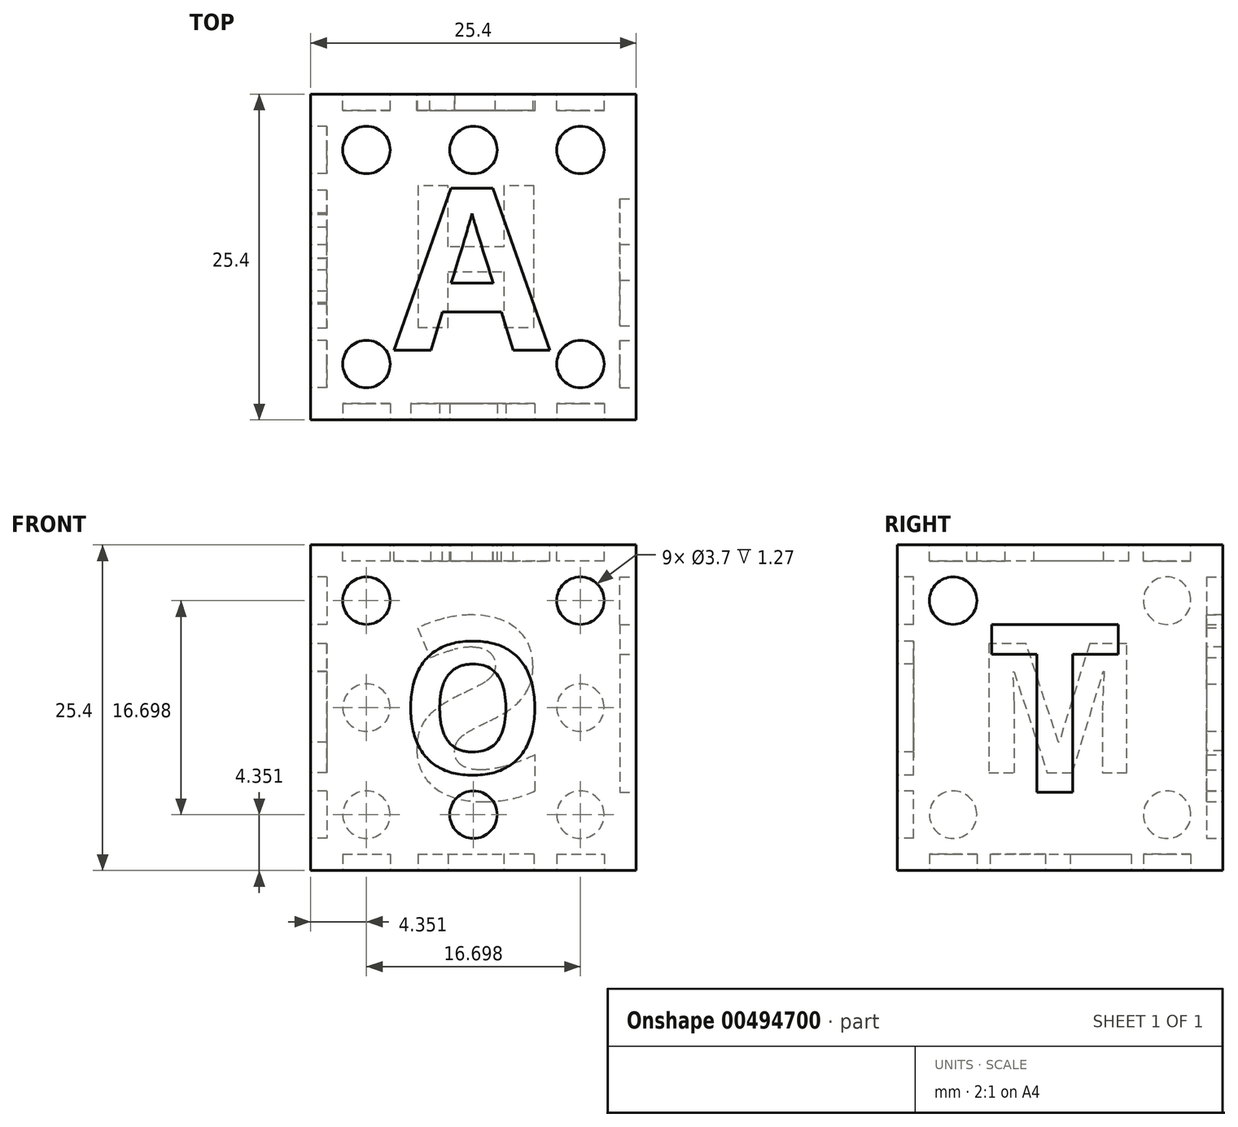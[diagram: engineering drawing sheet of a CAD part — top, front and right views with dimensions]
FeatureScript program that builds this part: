
annotation { "Feature Type Name" : "Feature", "Feature Type Description" : "" }
export const myFeature = defineFeature(function(context is Context, id is Id, definition is map)
    precondition{}
    {
        {
            var Q0;
            Q0=qCreatedBy(makeId("Top.planeOp"),FACE);
            var sketch = newSketch(context, id + "F0", { "sketchPlane" : qUnion([Q0])});
            skLineSegment(sketch, "E0.bottom", {"start": v(0, 0) * mm, "end": v(25.4, 0) * mm});
            skLineSegment(sketch, "E0.top", {"start": v(0, -25.4) * mm, "end": v(25.4, -25.4) * mm});
            skLineSegment(sketch, "E0.left", {"start": v(0, 0) * mm, "end": v(0, -25.4) * mm});
            skLineSegment(sketch, "E0.right", {"start": v(25.4, 0) * mm, "end": v(25.4, -25.4) * mm});
            skSolve(sketch);
        }
        {
            var Q0;
            Q0 = qSketchRegion(id + "F0", true);
            extrude(context, id + "F1", {"entities" : qUnion([Q0]), "depth" : 25.4 * mm});
        }
        {
            var Q0;
            Q0=makeQuery(id+"F1.opExtrude","SWEPT_FACE",FACE,{"disambiguationData":[OSD([sQuery(id+"F0.wireOp",EDGE,"E0.right")])]});
            var sketch = newSketch(context, id + "F2", { "sketchPlane" : qUnion([Q0])});
            skText(sketch, "E1", { "text": "T", "fontName": "OpenSans-Bold.ttf"});
            skLineSegment(sketch, "E2", {"start": v(-6.99, 12.7) * mm, "end": v(0, 12.7) * mm, "construction": true});
            skLineSegment(sketch, "E3", {"start": v(-12.7, 19.3) * mm, "end": v(-12.7, 25.4) * mm, "construction": true});
            skLineSegment(sketch, "E4", {"start": v(-18.42, 8.45) * mm, "end": v(-25.4, 8.45) * mm, "construction": true});
            skLineSegment(sketch, "E5", {"start": v(-12.7, 6.1) * mm, "end": v(-12.7, 0) * mm, "construction": true});
            skCircle(sketch, "E6", {"center": v(-21.05, 21.05) * mm, "radius": 1.85 * mm});
            skLineSegment(sketch, "E7.bottom", {"start": v(-22.9, 22.9) * mm, "end": v(-2.5, 22.9) * mm, "construction": true});
            skLineSegment(sketch, "E7.top", {"start": v(-22.9, 2.5) * mm, "end": v(-2.5, 2.5) * mm, "construction": true});
            skLineSegment(sketch, "E7.left", {"start": v(-22.9, 22.9) * mm, "end": v(-22.9, 2.5) * mm, "construction": true});
            skLineSegment(sketch, "E7.right", {"start": v(-2.5, 22.9) * mm, "end": v(-2.5, 2.5) * mm, "construction": true});
            const initialGuessF2  = {"E1": [-0.01842, 0.0061, 1, 0, 0.0132]};
            skSetInitialGuess(sketch, initialGuessF2);
            skSolve(sketch);
        }
        {
            var Q0;
            Q0=makeQuery(id+"F1.opExtrude","CAP_FACE",FACE,{"disambiguationData":[OSD([sQuery(id+"F0.wireOp",EDGE,"E0.bottom"),sQuery(id+"F0.wireOp",EDGE,"E0.top"),sQuery(id+"F0.wireOp",EDGE,"E0.left"),sQuery(id+"F0.wireOp",EDGE,"E0.right")])],"isStart":true});
            var sketch = newSketch(context, id + "F3", { "sketchPlane" : qUnion([Q0])});
            skText(sketch, "E8", { "text": "H", "fontName": "OpenSans-Bold.ttf"});
            skLineSegment(sketch, "E9", {"start": v(18.41, 12.7) * mm, "end": v(25.4, 12.7) * mm, "construction": true});
            skPoint(sketch, "E9.startSnap0", {"position": v(25.4, 12.7) * mm});
            skLineSegment(sketch, "E10", {"start": v(6.98, 12.7) * mm, "end": v(0, 12.7) * mm, "construction": true});
            skPoint(sketch, "E10.startSnap0", {"position": v(6.98, 12.7) * mm});
            skLineSegment(sketch, "E11", {"start": v(12.7, 18.26) * mm, "end": v(12.7, 25.4) * mm, "construction": true});
            skLineSegment(sketch, "E12", {"start": v(12.7, 25.4) * mm, "end": v(12.74, 25.95) * mm, "construction": true});
            skLineSegment(sketch, "E13", {"start": v(12.7, 7.14) * mm, "end": v(12.7, 0) * mm, "construction": true});
            skCircle(sketch, "E14", {"center": v(4.35, 21.05) * mm, "radius": 1.85 * mm});
            skCircle(sketch, "E15", {"center": v(21.05, 4.35) * mm, "radius": 1.85 * mm});
            skLineSegment(sketch, "E16.bottom", {"start": v(2.5, 22.9) * mm, "end": v(22.9, 22.9) * mm, "construction": true});
            skLineSegment(sketch, "E16.top", {"start": v(2.5, 2.5) * mm, "end": v(22.9, 2.5) * mm, "construction": true});
            skLineSegment(sketch, "E16.left", {"start": v(2.5, 22.9) * mm, "end": v(2.5, 2.5) * mm, "construction": true});
            skLineSegment(sketch, "E16.right", {"start": v(22.9, 22.9) * mm, "end": v(22.9, 2.5) * mm, "construction": true});
            const initialGuessF3  = {"E8": [0.00698, 0.00714, 1, 0, 0.01113]};
            skSetInitialGuess(sketch, initialGuessF3);
            skSolve(sketch);
        }
        {
            var Q0;
            Q0=makeQuery(id+"F1.opExtrude","SWEPT_FACE",FACE,{"disambiguationData":[OSD([sQuery(id+"F0.wireOp",EDGE,"E0.top")])]});
            var sketch = newSketch(context, id + "F4", { "sketchPlane" : qUnion([Q0])});
            skText(sketch, "E17", { "text": "O", "fontName": "OpenSans-Bold.ttf"});
            skLineSegment(sketch, "E18", {"start": v(12.7, 17.83) * mm, "end": v(12.7, 25.4) * mm, "construction": true});
            skLineSegment(sketch, "E19", {"start": v(18.41, 12.7) * mm, "end": v(25.4, 12.7) * mm, "construction": true});
            skLineSegment(sketch, "E20", {"start": v(25.4, 12.7) * mm, "end": v(25.78, 13.36) * mm, "construction": true});
            skLineSegment(sketch, "E21", {"start": v(12.7, 7.57) * mm, "end": v(12.7, 0) * mm, "construction": true});
            skLineSegment(sketch, "E22", {"start": v(12.7, 0) * mm, "end": v(12.7, -0.66) * mm, "construction": true});
            skLineSegment(sketch, "E23", {"start": v(6.98, 12.7) * mm, "end": v(0, 12.7) * mm, "construction": true});
            skCircle(sketch, "E24", {"center": v(4.35, 21.05) * mm, "radius": 1.85 * mm});
            skCircle(sketch, "E25", {"center": v(21.05, 21.05) * mm, "radius": 1.85 * mm});
            skPoint(sketch, "E26", {"position": v(12.7, 21.61) * mm});
            skLineSegment(sketch, "E27.top", {"start": v(4.64, 25.4) * mm, "end": v(0, 25.4) * mm, "construction": true});
            skLineSegment(sketch, "E27.right", {"start": v(0, 21.61) * mm, "end": v(0, 25.4) * mm, "construction": true});
            skLineSegment(sketch, "E28.top", {"start": v(20.76, 25.4) * mm, "end": v(25.4, 25.4) * mm, "construction": true});
            skLineSegment(sketch, "E28.right", {"start": v(25.4, 21.61) * mm, "end": v(25.4, 25.4) * mm, "construction": true});
            skCircle(sketch, "E29", {"center": v(12.7, 4.35) * mm, "radius": 1.85 * mm});
            skPoint(sketch, "E30.firstSnap0", {"position": v(2.5, 20.98) * mm});
            skLineSegment(sketch, "E30.bottom", {"start": v(2.5, 22.9) * mm, "end": v(22.9, 22.9) * mm, "construction": true});
            skLineSegment(sketch, "E30.top", {"start": v(2.5, 2.5) * mm, "end": v(22.9, 2.5) * mm, "construction": true});
            skLineSegment(sketch, "E30.left", {"start": v(2.5, 22.9) * mm, "end": v(2.5, 2.5) * mm, "construction": true});
            skLineSegment(sketch, "E30.right", {"start": v(22.9, 22.9) * mm, "end": v(22.9, 2.5) * mm, "construction": true});
            const initialGuessF4  = {"E17": [0.00698, 0.00757, 1, 0, 0.01025]};
            skSetInitialGuess(sketch, initialGuessF4);
            skSolve(sketch);
        }
        {
            var Q0;
            Q0=makeQuery(id+"F1.opExtrude","SWEPT_FACE",FACE,{"disambiguationData":[OSD([sQuery(id+"F0.wireOp",EDGE,"E0.left")])]});
            var sketch = newSketch(context, id + "F5", { "sketchPlane" : qUnion([Q0])});
            skText(sketch, "E31", { "text": "M", "fontName": "OpenSans-Bold.ttf"});
            skLineSegment(sketch, "E32", {"start": v(12.7, 17.78) * mm, "end": v(12.7, 25.4) * mm, "construction": true});
            skLineSegment(sketch, "E33", {"start": v(19.18, 7.17) * mm, "end": v(25.4, 7.17) * mm, "construction": true});
            skLineSegment(sketch, "E34", {"start": v(6.22, 7.17) * mm, "end": v(0, 7.17) * mm, "construction": true});
            skLineSegment(sketch, "E35", {"start": v(12.7, 7.62) * mm, "end": v(12.7, 0) * mm, "construction": true});
            skCircle(sketch, "E36", {"center": v(21.05, 21.05) * mm, "radius": 1.85 * mm});
            skCircle(sketch, "E37", {"center": v(4.35, 21.05) * mm, "radius": 1.85 * mm});
            skCircle(sketch, "E38", {"center": v(4.35, 4.35) * mm, "radius": 1.85 * mm});
            skCircle(sketch, "E39", {"center": v(21.05, 4.35) * mm, "radius": 1.85 * mm});
            skLineSegment(sketch, "E40", {"start": v(0, 20.74) * mm, "end": v(0.09, 21.93) * mm, "construction": true});
            skLineSegment(sketch, "E41", {"start": v(25.4, 4.66) * mm, "end": v(25.62, 3.31) * mm, "construction": true});
            skPoint(sketch, "E42.oppositeSnap0", {"position": v(22.9, 4.66) * mm});
            skLineSegment(sketch, "E42.bottom", {"start": v(2.5, 22.9) * mm, "end": v(22.9, 22.9) * mm, "construction": true});
            skLineSegment(sketch, "E42.top", {"start": v(2.5, 2.5) * mm, "end": v(22.9, 2.5) * mm, "construction": true});
            skLineSegment(sketch, "E42.left", {"start": v(2.5, 22.9) * mm, "end": v(2.5, 2.5) * mm, "construction": true});
            skLineSegment(sketch, "E42.right", {"start": v(22.9, 22.9) * mm, "end": v(22.9, 2.5) * mm, "construction": true});
            const initialGuessF5  = {"E31": [0.00622, 0.00762, 1, 0, 0.01016]};
            skSetInitialGuess(sketch, initialGuessF5);
            skSolve(sketch);
        }
        {
            var Q0;
            Q0=makeQuery(id+"F1.opExtrude","CAP_FACE",FACE,{"disambiguationData":[OSD([sQuery(id+"F0.wireOp",EDGE,"E0.bottom"),sQuery(id+"F0.wireOp",EDGE,"E0.top"),sQuery(id+"F0.wireOp",EDGE,"E0.left"),sQuery(id+"F0.wireOp",EDGE,"E0.right")])],"isStart":false});
            var sketch = newSketch(context, id + "F6", { "sketchPlane" : qUnion([Q0])});
            skText(sketch, "E43", { "text": "A", "fontName": "OpenSans-Bold.ttf"});
            skCircle(sketch, "E44", {"center": v(21.05, -4.35) * mm, "radius": 1.85 * mm});
            skCircle(sketch, "E45", {"center": v(4.35, -4.35) * mm, "radius": 1.85 * mm});
            skCircle(sketch, "E46", {"center": v(12.7, -4.35) * mm, "radius": 1.85 * mm});
            skCircle(sketch, "E47", {"center": v(4.35, -21.05) * mm, "radius": 1.85 * mm});
            skCircle(sketch, "E48", {"center": v(21.05, -21.05) * mm, "radius": 1.85 * mm});
            skPoint(sketch, "E49", {"position": v(21.05, -12.02) * mm});
            skLineSegment(sketch, "E50.bottom", {"start": v(2.5, -2.5) * mm, "end": v(22.9, -2.5) * mm, "construction": true});
            skLineSegment(sketch, "E50.top", {"start": v(2.5, -22.9) * mm, "end": v(22.9, -22.9) * mm, "construction": true});
            skLineSegment(sketch, "E50.left", {"start": v(2.5, -2.5) * mm, "end": v(2.5, -22.9) * mm, "construction": true});
            skLineSegment(sketch, "E50.right", {"start": v(22.9, -2.5) * mm, "end": v(22.9, -22.9) * mm, "construction": true});
            const initialGuessF6  = {"E43": [0.0065, -0.01998, 1, 0, 0.0127]};
            skSetInitialGuess(sketch, initialGuessF6);
            skSolve(sketch);
        }
        {
            var Q0;
            Q0=makeQuery(id+"F1.opExtrude","SWEPT_FACE",FACE,{"disambiguationData":[OSD([sQuery(id+"F0.wireOp",EDGE,"E0.bottom")])]});
            var sketch = newSketch(context, id + "F7", { "sketchPlane" : qUnion([Q0])});
            skText(sketch, "E51", { "text": "S", "fontName": "OpenSans-Bold.ttf"});
            skLineSegment(sketch, "E52", {"start": v(-25.4, 12.7) * mm, "end": v(-25.57, 13.09) * mm, "construction": true});
            skCircle(sketch, "E53", {"center": v(-21.05, 21.05) * mm, "radius": 1.85 * mm});
            skCircle(sketch, "E54", {"center": v(-4.35, 21.05) * mm, "radius": 1.85 * mm});
            skCircle(sketch, "E55", {"center": v(-4.35, 12.7) * mm, "radius": 1.85 * mm});
            skCircle(sketch, "E56", {"center": v(-21.05, 4.35) * mm, "radius": 1.85 * mm});
            skCircle(sketch, "E57", {"center": v(-4.35, 4.35) * mm, "radius": 1.85 * mm});
            skCircle(sketch, "E58", {"center": v(-21.05, 12.7) * mm, "radius": 1.85 * mm});
            skLineSegment(sketch, "E59.bottom", {"start": v(-22.9, 22.9) * mm, "end": v(-2.5, 22.9) * mm, "construction": true});
            skLineSegment(sketch, "E59.top", {"start": v(-22.9, 2.5) * mm, "end": v(-2.5, 2.5) * mm, "construction": true});
            skLineSegment(sketch, "E59.left", {"start": v(-22.9, 22.9) * mm, "end": v(-22.9, 2.5) * mm, "construction": true});
            skLineSegment(sketch, "E59.right", {"start": v(-2.5, 22.9) * mm, "end": v(-2.5, 2.5) * mm, "construction": true});
            skLineSegment(sketch, "E60", {"start": v(0, 12.7) * mm, "end": v(-25.4, 12.7) * mm, "construction": true});
            const initialGuessF7  = {"E51": [-0.01842, 0.00556, 1, 0, 0.01429]};
            skSetInitialGuess(sketch, initialGuessF7);
            skSolve(sketch);
        }
        {
            var Q0;
            Q0 = qSketchRegion(id + "F2", true);
            extrude(context, id + "F8", {"entities" : qUnion([Q0]), "operationType" : NewBodyOperationType.REMOVE, "oppositeDirection" : true, "depth" : 1.27 * mm});
        }
        {
            var Q0;
            Q0=makeQuery(id+"F7.imprint","IMPRINT",FACE,{"disambiguationData":[TD([[makeQuery(id+"F7.imprint","IMPRINT",EDGE,{"derivedFrom":sQuery(id+"F7.wireOp",EDGE,"E51.sketch_text.stroke-0")}),-1.0]])]});
            var Q1;
            Q1=makeQuery(id+"F7.imprint","IMPRINT",FACE,{"disambiguationData":[TD([[makeQuery(id+"F7.imprint","IMPRINT",EDGE,{"derivedFrom":sQuery(id+"F7.wireOp",EDGE,"E55")}),1.0]])]});
            var Q2;
            Q2=makeQuery(id+"F7.imprint","IMPRINT",FACE,{"disambiguationData":[TD([[makeQuery(id+"F7.imprint","IMPRINT",EDGE,{"derivedFrom":sQuery(id+"F7.wireOp",EDGE,"E58")}),1.0]])]});
            var Q3;
            Q3=makeQuery(id+"F7.imprint","IMPRINT",FACE,{"disambiguationData":[TD([[makeQuery(id+"F7.imprint","IMPRINT",EDGE,{"derivedFrom":sQuery(id+"F7.wireOp",EDGE,"E56")}),1.0]])]});
            var Q4;
            Q4=makeQuery(id+"F7.imprint","IMPRINT",FACE,{"disambiguationData":[TD([[makeQuery(id+"F7.imprint","IMPRINT",EDGE,{"derivedFrom":sQuery(id+"F7.wireOp",EDGE,"E53")}),1.0]])]});
            var Q5;
            Q5=makeQuery(id+"F7.imprint","IMPRINT",FACE,{"disambiguationData":[TD([[makeQuery(id+"F7.imprint","IMPRINT",EDGE,{"derivedFrom":sQuery(id+"F7.wireOp",EDGE,"E54")}),1.0]])]});
            var Q6;
            Q6=makeQuery(id+"F7.imprint","IMPRINT",FACE,{"disambiguationData":[TD([[makeQuery(id+"F7.imprint","IMPRINT",EDGE,{"derivedFrom":sQuery(id+"F7.wireOp",EDGE,"E57")}),1.0]])]});
            extrude(context, id + "F9", {"entities" : qUnion([Q0, Q1, Q2, Q3, Q4, Q5, Q6]), "operationType" : NewBodyOperationType.REMOVE, "oppositeDirection" : true, "depth" : 1.27 * mm});
        }
        {
            var Q0;
            Q0=makeQuery(id+"F6.imprint","IMPRINT",FACE,{"disambiguationData":[TD([[makeQuery(id+"F6.imprint","IMPRINT",EDGE,{"derivedFrom":sQuery(id+"F6.wireOp",EDGE,"E48")}),1.0]])]});
            var Q1;
            Q1=makeQuery(id+"F6.imprint","IMPRINT",FACE,{"disambiguationData":[TD([[makeQuery(id+"F6.imprint","IMPRINT",EDGE,{"derivedFrom":sQuery(id+"F6.wireOp",EDGE,"E44")}),1.0]])]});
            var Q2;
            Q2=makeQuery(id+"F6.imprint","IMPRINT",FACE,{"disambiguationData":[TD([[makeQuery(id+"F6.imprint","IMPRINT",EDGE,{"derivedFrom":sQuery(id+"F6.wireOp",EDGE,"E46")}),1.0]])]});
            var Q3;
            Q3=makeQuery(id+"F6.imprint","IMPRINT",FACE,{"disambiguationData":[TD([[makeQuery(id+"F6.imprint","IMPRINT",EDGE,{"derivedFrom":sQuery(id+"F6.wireOp",EDGE,"E45")}),1.0]])]});
            var Q4;
            Q4=makeQuery(id+"F6.imprint","IMPRINT",FACE,{"disambiguationData":[TD([[makeQuery(id+"F6.imprint","IMPRINT",EDGE,{"derivedFrom":sQuery(id+"F6.wireOp",EDGE,"E43.sketch_text.stroke-0")}),-1.0]])]});
            var Q5;
            Q5=makeQuery(id+"F6.imprint","IMPRINT",FACE,{"disambiguationData":[TD([[makeQuery(id+"F6.imprint","IMPRINT",EDGE,{"derivedFrom":sQuery(id+"F6.wireOp",EDGE,"E47")}),1.0]])]});
            extrude(context, id + "F10", {"entities" : qUnion([Q0, Q1, Q2, Q3, Q4, Q5]), "operationType" : NewBodyOperationType.REMOVE, "oppositeDirection" : true, "depth" : 1.27 * mm});
        }
        {
            var Q0;
            Q0=makeQuery(id+"F3.imprint","IMPRINT",FACE,{"disambiguationData":[TD([[makeQuery(id+"F3.imprint","IMPRINT",EDGE,{"derivedFrom":sQuery(id+"F3.wireOp",EDGE,"E8.sketch_text.stroke-0")}),-1.0]])]});
            var Q1;
            Q1=makeQuery(id+"F3.imprint","IMPRINT",FACE,{"disambiguationData":[TD([[makeQuery(id+"F3.imprint","IMPRINT",EDGE,{"derivedFrom":sQuery(id+"F3.wireOp",EDGE,"E15")}),1.0]])]});
            var Q2;
            Q2=makeQuery(id+"F3.imprint","IMPRINT",FACE,{"disambiguationData":[TD([[makeQuery(id+"F3.imprint","IMPRINT",EDGE,{"derivedFrom":sQuery(id+"F3.wireOp",EDGE,"E14")}),1.0]])]});
            extrude(context, id + "F11", {"entities" : qUnion([Q0, Q1, Q2]), "operationType" : NewBodyOperationType.REMOVE, "oppositeDirection" : true, "depth" : 1.27 * mm});
        }
        {
            var Q0;
            Q0=makeQuery(id+"F5.imprint","IMPRINT",FACE,{"disambiguationData":[TD([[makeQuery(id+"F5.imprint","IMPRINT",EDGE,{"derivedFrom":sQuery(id+"F5.wireOp",EDGE,"E38")}),1.0]])]});
            var Q1;
            Q1=makeQuery(id+"F5.imprint","IMPRINT",FACE,{"disambiguationData":[TD([[makeQuery(id+"F5.imprint","IMPRINT",EDGE,{"derivedFrom":sQuery(id+"F5.wireOp",EDGE,"E39")}),1.0]])]});
            var Q2;
            Q2=makeQuery(id+"F5.imprint","IMPRINT",FACE,{"disambiguationData":[TD([[makeQuery(id+"F5.imprint","IMPRINT",EDGE,{"derivedFrom":sQuery(id+"F5.wireOp",EDGE,"E37")}),1.0]])]});
            var Q3;
            Q3=makeQuery(id+"F5.imprint","IMPRINT",FACE,{"disambiguationData":[TD([[makeQuery(id+"F5.imprint","IMPRINT",EDGE,{"derivedFrom":sQuery(id+"F5.wireOp",EDGE,"E36")}),1.0]])]});
            var Q4;
            Q4=makeQuery(id+"F5.imprint","IMPRINT",FACE,{"disambiguationData":[TD([[makeQuery(id+"F5.imprint","IMPRINT",EDGE,{"derivedFrom":sQuery(id+"F5.wireOp",EDGE,"E31.sketch_text.stroke-0")}),-1.0]])]});
            extrude(context, id + "F12", {"entities" : qUnion([Q0, Q1, Q2, Q3, Q4]), "operationType" : NewBodyOperationType.REMOVE, "oppositeDirection" : true, "depth" : 1.27 * mm});
        }
        {
            var Q0;
            Q0=makeQuery(id+"F4.imprint","IMPRINT",FACE,{"disambiguationData":[TD([[makeQuery(id+"F4.imprint","IMPRINT",EDGE,{"derivedFrom":sQuery(id+"F4.wireOp",EDGE,"E17.sketch_text.stroke-0")}),-1.0]])]});
            var Q1;
            Q1=makeQuery(id+"F4.imprint","IMPRINT",FACE,{"disambiguationData":[TD([[makeQuery(id+"F4.imprint","IMPRINT",EDGE,{"derivedFrom":sQuery(id+"F4.wireOp",EDGE,"E29")}),1.0]])]});
            var Q2;
            Q2=makeQuery(id+"F4.imprint","IMPRINT",FACE,{"disambiguationData":[TD([[makeQuery(id+"F4.imprint","IMPRINT",EDGE,{"derivedFrom":sQuery(id+"F4.wireOp",EDGE,"E24")}),1.0]])]});
            var Q3;
            Q3=makeQuery(id+"F4.imprint","IMPRINT",FACE,{"disambiguationData":[TD([[makeQuery(id+"F4.imprint","IMPRINT",EDGE,{"derivedFrom":sQuery(id+"F4.wireOp",EDGE,"E25")}),1.0]])]});
            extrude(context, id + "F13", {"entities" : qUnion([Q0, Q1, Q2, Q3]), "operationType" : NewBodyOperationType.REMOVE, "oppositeDirection" : true, "depth" : 1.27 * mm});
        }
    });
